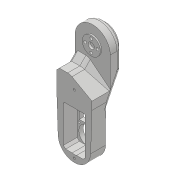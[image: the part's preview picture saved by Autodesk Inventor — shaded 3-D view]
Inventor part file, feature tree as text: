
AUTODESK INVENTOR PART (.ipt)
format: ipt  version: 2018 (Build 220112000, 112)  size: 977,920 bytes
history: native  units: mm
features: projected_geometry x42, sketch x41, extrude x34, fillet x13, chamfer x11, hole x8, other x4, mirror x1, reference x1
ambient origin geometry x8: Origin, YZ Plane, XZ Plane, XY Plane, X Axis, Y Axis, Z Axis, Center Point
bodies: Solid1 (feature_tree)
feature tree (155):
  extrude  "Extrusion1"  Depth=45.0mm
  extrude  "Extrusion2"  Depth=2.25mm
  hole  "Hole1"  [1 undecoded]
  hole  "Hole2"  [1 undecoded]
  fillet  "Fillet1"  Radius=14.0mm
  extrude  "Extrusion3"  Depth=18.5mm
  extrude  "Extrusion4"  Depth=10.0mm
  extrude  "Extrusion5"  Depth=2.195mm
  extrude  "Extrusion6"  Depth=20.5mm
  hole  "Hole3"  [1 undecoded]
  extrude  "Extrusion7"  Depth=0.5mm
  extrude  "Extrusion8"  Depth=5.0mm TaperAngle=0.0deg
  extrude  "Extrusion9"  Depth=10.0mm
  extrude  "Extrusion10"  Depth=10.0mm
  extrude  "Extrusion11"  Depth=14.5mm
  extrude  "Extrusion12"  Depth=14.5mm
  extrude  "Extrusion13"  Depth=5.0mm
  extrude  "Extrusion14"  Depth=5.0mm
  extrude  "Extrusion15"  Depth=5.0mm
  extrude  "Extrusion16"  Depth=5.0mm
  extrude  "Extrusion17"  Depth=4.0mm
  chamfer  "Chamfer1"  Distance=1.0mm
  fillet  "Fillet7"  Radius=20.7mm
  fillet  "Fillet8"  Radius=32.0mm
  mirror  "Mirror1"
  extrude  "Extrusion19"  Depth=5.0mm TaperAngle=0.0deg
  extrude  "Extrusion20"  Depth=8.0mm
  extrude  "Extrusion21"  Depth=0.2mm TaperAngle=0.0deg
  extrude  "Extrusion22"  Depth=0.5mm TaperAngle=0.0deg
  extrude  "Extrusion23"  Depth=9.0mm TaperAngle=0.0deg
  extrude  "Extrusion24"  Depth=5.0mm TaperAngle=0.0deg
  chamfer  "Chamfer2"  Distance=0.2mm
  chamfer  "Chamfer8"  Distance=2.5mm Angle=45.0deg
  extrude  "Extrusion25"  Depth=0.5mm
  extrude  "Extrusion26"  Depth=2.0mm TaperAngle=0.0deg
  chamfer  "Chamfer3"  Distance=2.0mm
  chamfer  "Chamfer4"  Distance=2.0mm
  chamfer  "Chamfer5"  Distance=15.0mm
  chamfer  "Chamfer6"  Distance=56.1mm
  fillet  "Fillet9"  Radius=41.6mm
  fillet  "Fillet10"  Radius=41.0mm
  hole  "Hole6"  [1 undecoded]
  fillet  "Fillet12"  Radius=7.0mm
  hole  "Hole7"  [1 undecoded]
  extrude  "Extrusion27"  Depth=3.0mm TaperAngle=45.0deg
  extrude  "Extrusion28"  Depth=5.0mm TaperAngle=45.0deg
  hole  "Hole8"  [1 undecoded]
  extrude  "Extrusion29"  Depth=10.0mm
  chamfer  "Chamfer7"  Distance=20.5mm
  fillet  "Fillet13"  Radius=1.6mm
  extrude  "Extrusion30"  Depth=10.0mm
  extrude  "Extrusion31"  Depth=10.0mm TaperAngle=0.0deg
  fillet  "Fillet14"  Radius=14.0mm
  extrude  "Extrusion32"  Depth=10.0mm
  fillet  "Fillet15"  Radius=3.1mm
  fillet  "Fillet18"  Radius=1.5mm
  extrude  "Extrusion35"  Depth=10.0mm
  extrude  "Extrusion36"  Depth=10.0mm
  chamfer  "Chamfer9"  Distance=10.0mm
  chamfer  "Chamfer10"  Distance=7.5mm
  chamfer  "Chamfer11"  Distance=6.0mm
  fillet  "Fillet19"  Radius=6.0mm
  hole  "Hole9"  [1 undecoded]
  fillet  "Fillet20"  Radius=6.0mm
  hole  "Hole10"  [1 undecoded]
  fillet  "Fillet21"  Radius=1.5mm
  extrude  "Extrusion37"  Depth=10.0mm
  sketch  "Sketch1"  dims[d0=24.5mm d1=45.0mm]
  sketch  "Sketch2"  dims[d2=1.95mm d3=0.0mm d4=2.25mm]
  projected_geometry  "Projected Loop1"
  sketch  "Sketch3"  dims[d5=20.0mm d6=2.25mm]
  projected_geometry  "Projected Loop2"
  sketch  "Sketch4"  dims[d7=5.25mm d8=5.25mm d9=14.0mm]
  projected_geometry  "Projected Loop3"
  sketch  "Sketch5"  dims[d10=5.25mm d11=18.5mm]
  projected_geometry  "Projected Loop4"
  sketch  "Sketch6"  dims[d12=10.0mm d13=0.0mm d14=20.5mm]
  projected_geometry  "Projected Loop5"
  sketch  "Sketch7"  dims[d15=2.0mm d16=2.195mm]
  projected_geometry  "Projected Loop6"
  sketch  "Sketch8"  dims[d17=2.0mm]
  projected_geometry  "Projected Loop7"
  sketch  "Sketch9"  dims[d18=2.4mm d19=6.0mm d20=4.4mm d21=2.0mm d22=90.0deg d23=8.0mm d24=20.594885mm d25=20.5mm]
  projected_geometry  "Projected Loop8"
  projected_geometry  "Projected Loop9"
  sketch  "Sketch10"  dims[d26=26.65mm d27=2.0mm]
  projected_geometry  "Projected Loop10"
  projected_geometry  "Projected Loop11"
  sketch  "Sketch11"  dims[d28=2.0mm]
  projected_geometry  "Projected Loop12"
  sketch  "Sketch12"  dims[d29=2.4mm d30=6.0mm d31=4.4mm d32=2.0mm d33=90.0deg d34=8.0mm d35=20.594885mm d36=0.5mm]
  sketch  "Sketch13"  dims[d37=18.0mm d38=5.0mm d39=0.0mm]
  sketch  "Sketch14"  dims[d41=10.0mm d42=0.0mm d43=24.5mm]
  projected_geometry  "Projected Loop13"
  sketch  "Sketch15"  dims[d44=1.15mm d45=0.0mm d46=10.0mm]
  sketch  "Sketch16"  dims[d47=21.0mm d48=14.5mm]
  projected_geometry  "Projected Loop14"
  sketch  "Sketch17"  dims[d49=20.0mm d50=14.5mm]
  projected_geometry  "Projected Loop15"
  sketch  "Sketch18"  dims[d51=24.5mm d52=5.0mm]
  projected_geometry  "Projected Loop16"
  sketch  "Sketch19"  dims[d53=5.0mm d54=2.25mm]
  projected_geometry  "Projected Loop17"
  sketch  "Sketch20"  dims[d55=2.25mm d56=5.0mm]
  projected_geometry  "Projected Loop18"
  sketch  "Sketch25"  dims[d57=5.0mm d58=9.0mm]
  projected_geometry  "Projected Loop22"
  sketch  "Sketch26"  dims[d59=14.75mm d60=4.0mm d61=1.0mm d62=0.0mm d63=20.7mm]
  projected_geometry  "Projected Loop23"
  sketch  "Sketch27"  dims[d64=2.4mm d65=6.0mm d66=4.4mm d67=2.0mm d68=90.0deg d69=8.0mm d70=20.594885mm d72=32.0mm]
  projected_geometry  "Projected Loop24"
  sketch  "Sketch28"  dims[d73=5.0mm d74=0.0mm d75=1.0mm d76=0.0mm]
  projected_geometry  "Projected Loop25"
  sketch  "Sketch29"  dims[d77=12.25mm d78=0.0mm d80=8.0mm]
  projected_geometry  "Projected Loop26"
  sketch  "Sketch30"  dims[d81=4.5mm d82=0.0mm d84=0.2mm d85=0.0mm]
  projected_geometry  "Projected Loop27"
  sketch  "Sketch31"  dims[d86=21.0mm d87=0.5mm d88=0.0mm]
  sketch  "Sketch33"  dims[d91=8.0mm d92=0.0mm d93=9.0mm d94=0.0mm]
  projected_geometry  "Projected Loop28"
  projected_geometry  "Projected Loop29"
  projected_geometry  "Projected Loop30"
  sketch  "Sketch34"  dims[d95=5.0mm d96=0.0mm d98=0.2mm d99=0.0mm d100=0.2mm d101=0.0mm d102=2.5mm d103=2.0mm d104=45.0deg]
  projected_geometry  "Projected Loop31"
  projected_geometry  "Projected Loop32"
  sketch  "Sketch35"  dims[d105=1.5mm d114=0.5mm]
  projected_geometry  "Projected Loop33"
  sketch  "Sketch36"  dims[d128=2.0mm d129=0.0mm d130=2.0mm d131=0.0mm]
  projected_geometry  "Projected Loop34"
  sketch  "Sketch37"  dims[d132=40.0mm d133=2.0mm d134=0.0mm d135=2.0mm d136=0.0mm]
  projected_geometry  "Projected Loop35"
  sketch  "Sketch38"  dims[d137=40.0mm]
  projected_geometry  "Projected Loop36"
  sketch  "Sketch39"  dims[d138=70.0mm d139=15.0mm d140=0.0mm d141=56.1mm d142=0.0mm]
  projected_geometry  "Projected Loop37"
  sketch  "Sketch40"  dims[d143=4.0mm d144=8.0mm d145=45.0deg d146=41.6mm d147=41.0mm]
  projected_geometry  "Projected Loop38"
  sketch  "Sketch41"  dims[d148=7.0mm d149=7.0mm d150=7.0mm]
  projected_geometry  "Projected Loop39"
  reference  "Reference1"
  sketch  "Sketch44"  dims[d151=100.0mm d152=0.0mm d153=15.282752mm]
  projected_geometry  "Projected Loop42"
  sketch  "Sketch45"  dims[d156=100.0mm d157=0.0mm d158=3.0mm d159=2.0mm d160=45.0deg]
  projected_geometry  "Projected Loop43"
  sketch  "Sketch46"  dims[d161=5.0mm d162=2.0mm d163=45.0deg d164=5.0mm d165=2.0mm d166=45.0deg]
  projected_geometry  "Projected Loop44"
  sketch  "Sketch47"  dims[d167=5.0mm d168=2.0mm d169=45.0deg d170=5.0mm]
  projected_geometry  "Projected Loop45"
  sketch  "Sketch48"  dims[d171=2.0mm d173=5.7mm d174=6.0mm d175=4.0mm d176=2.0mm d177=90.0deg d178=25.0mm d179=0.0mm d180=1.0mm d181=2.459mm d182=25.0mm d183=4.0mm d184=2.0mm d185=90.0deg d186=25.0mm d187=20.594885mm d188=20.5mm d189=1.6mm d190=0.0mm d191=20.5mm d192=3.1mm d193=0.0mm d194=14.0mm d195=3.2mm d196=25.0mm d197=6.3mm d198=2.0mm d199=90.0deg d200=25.0mm d201=20.594885mm d202=16.0mm d203=3.1mm d204=0.0mm d205=1.5mm d206=2.0mm d207=45.0deg d208=1.7mm d209=37.0mm d210=10.0mm d211=0.0mm d212=7.5mm d213=6.0mm d214=6.0mm d215=6.0mm d216=6.0mm d217=5.0mm d218=0.0mm d219=1.5mm d220=6.0mm d221=6.0mm d222=6.0mm d223=6.0mm d224=6.0mm d225=0.0mm d226=1.5mm d231=4.0mm d232=8.0mm d233=45.0deg d234=10.0mm d237=7.0mm d238=2.5mm d239=0.0mm d240=7.0mm d241=2.5mm d242=0.0mm d243=14.0mm d244=25.0mm d245=45.0deg d246=14.0mm d247=25.0mm d248=45.0deg d249=14.0mm d250=25.0mm d251=45.0deg d252=10.0mm d253=4.0mm d254=6.0mm d255=4.0mm d256=2.0mm d257=90.0deg d258=2.0mm d259=20.594885mm d260=1.0mm d261=4.0mm d262=6.0mm d263=4.0mm d264=2.0mm d265=90.0deg d266=2.0mm d267=20.594885mm d268=1.0mm d269=35.55mm d270=0.0mm]
  projected_geometry  "Project Cut Edges1"
  projected_geometry  "Project Cut Edges2"
  parser-record x1  (decoder bookkeeping rows leaked as tree rows — omitted from the tree; the rows remain in map.json)
  other  "servocheck.iam"
  other  "bottomarm:1"
  other  "arm1:1"
note: 8 required parameter values undecoded (feature->parameter linkage not recoverable at this tier; creation-order binding heuristic only, values carry confidence <= 0.55)
note: 1 file-system path scrubbed to <path> (originals preserved in map.json)
